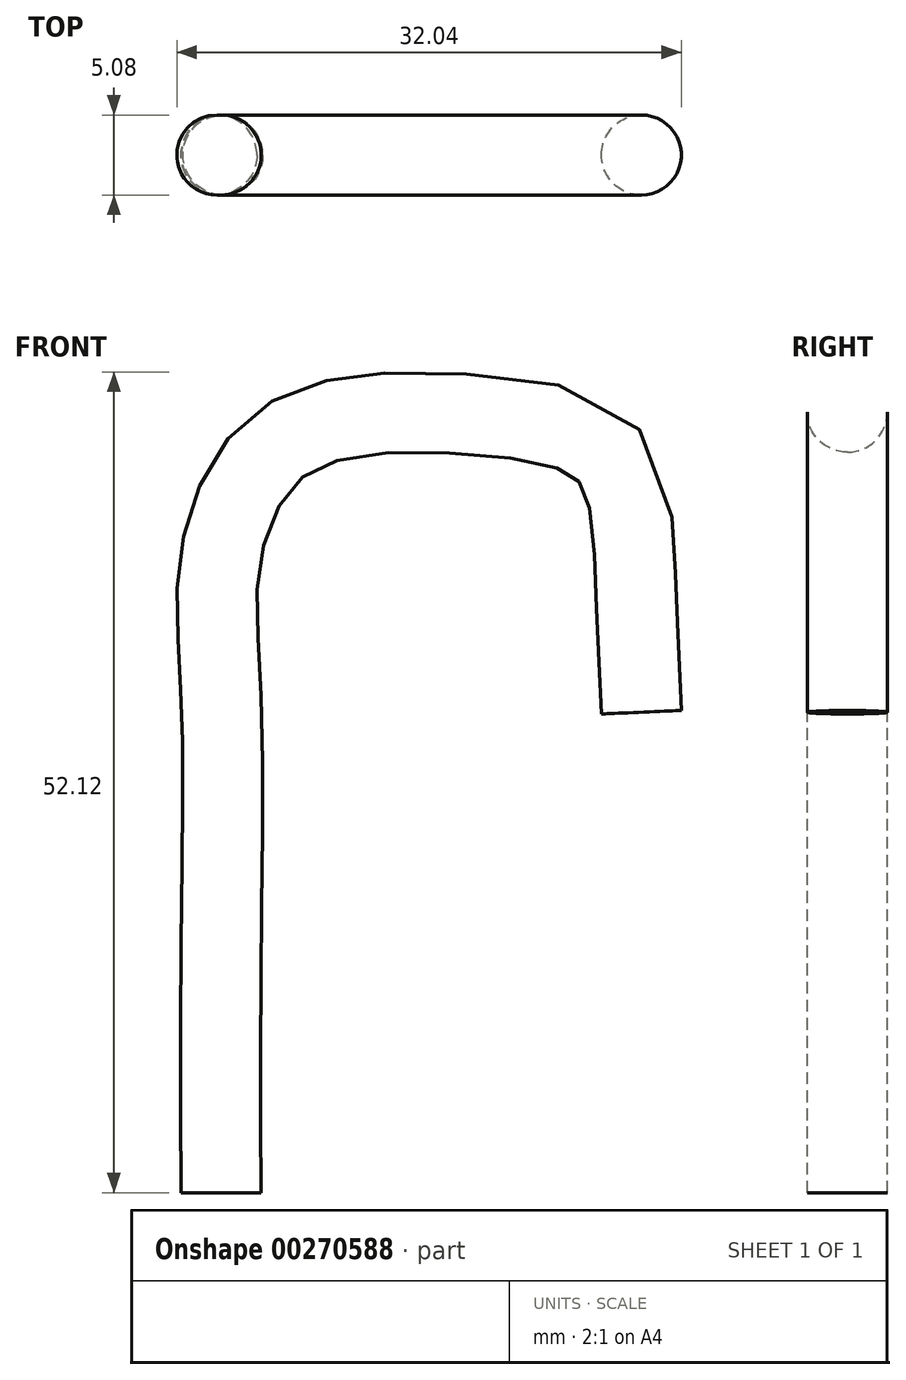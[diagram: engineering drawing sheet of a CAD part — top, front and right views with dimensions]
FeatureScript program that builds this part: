
annotation { "Feature Type Name" : "Feature", "Feature Type Description" : "" }
export const myFeature = defineFeature(function(context is Context, id is Id, definition is map)
    precondition{}
    {
        {
            var Q0;
            Q0=qCreatedBy(makeId("Top.planeOp"),FACE);
            var sketch = newSketch(context, id + "F0", { "sketchPlane" : qUnion([Q0])});
            skCircle(sketch, "E0", {"center": v(0, 0) * mm, "radius": 2.54 * mm});
            skSolve(sketch);
        }
        {
            var Q0;
            Q0=qCreatedBy(makeId("Front.planeOp"),FACE);
            var sketch = newSketch(context, id + "F1", { "sketchPlane" : qUnion([Q0])});
            skFitSpline(sketch, "E1", {"points": [v(0, 0) * mm, v(0, 16.06) * mm, v(0, 31.5) * mm, v(0, 40.67) * mm, v(4.23, 47.9) * mm, v(15.56, 49.46) * mm, v(24.54, 46.92) * mm, v(26.3, 39.3) * mm, v(26.7, 30.52) * mm], "startDerivative": vector(-0.58, 103.15) * mm, "endDerivative": vector(3.72, -75.8) * mm});
            skSolve(sketch);
        }
        {
            var Q0;
            Q0=makeQuery(id+"F0.imprint","IMPRINT",FACE,{"disambiguationData":[TD([[makeQuery(id+"F0.imprint","IMPRINT",EDGE,{"derivedFrom":sQuery(id+"F0.wireOp",EDGE,"E0")}),1.0]])]});
            var Q1;
            Q1=sQuery(id+"F1.wireOp",EDGE,"E1");
            sweep(context, id + "F2", {"profiles" : qUnion([Q0]), "path" : qUnion([Q1])});
        }
    });
